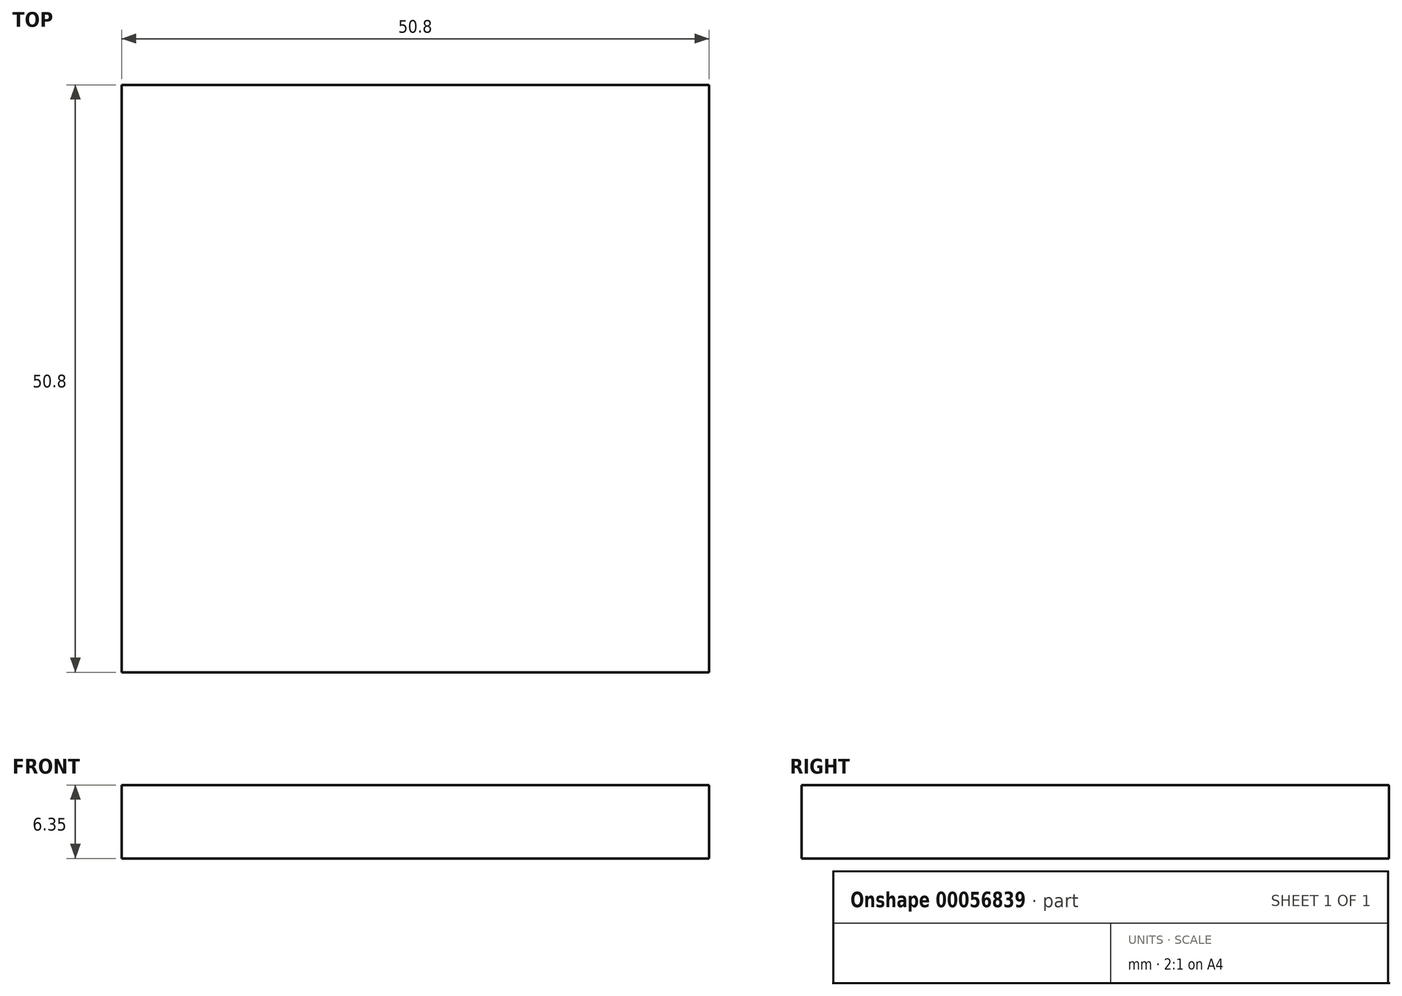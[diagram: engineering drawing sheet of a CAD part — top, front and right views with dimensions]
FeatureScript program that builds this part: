
annotation { "Feature Type Name" : "Feature", "Feature Type Description" : "" }
export const myFeature = defineFeature(function(context is Context, id is Id, definition is map)
    precondition{}
    {
        {
            var Q0;
            Q0=qCreatedBy(makeId("Top.planeOp"),FACE);
            var sketch = newSketch(context, id + "F0", { "sketchPlane" : qUnion([Q0])});
            skLineSegment(sketch, "E0.bottom", {"start": v(0, 0) * mm, "end": v(50.8, 0) * mm});
            skLineSegment(sketch, "E0.top", {"start": v(0, 50.8) * mm, "end": v(50.8, 50.8) * mm});
            skLineSegment(sketch, "E0.left", {"start": v(0, 0) * mm, "end": v(0, 50.8) * mm});
            skLineSegment(sketch, "E0.right", {"start": v(50.8, 0) * mm, "end": v(50.8, 50.8) * mm});
            skSolve(sketch);
        }
        {
            var Q0;
            Q0 = qSketchRegion(id + "F0", true);
            extrude(context, id + "F1", {"entities" : qUnion([Q0]), "depth" : 6.35 * mm});
        }
    });
